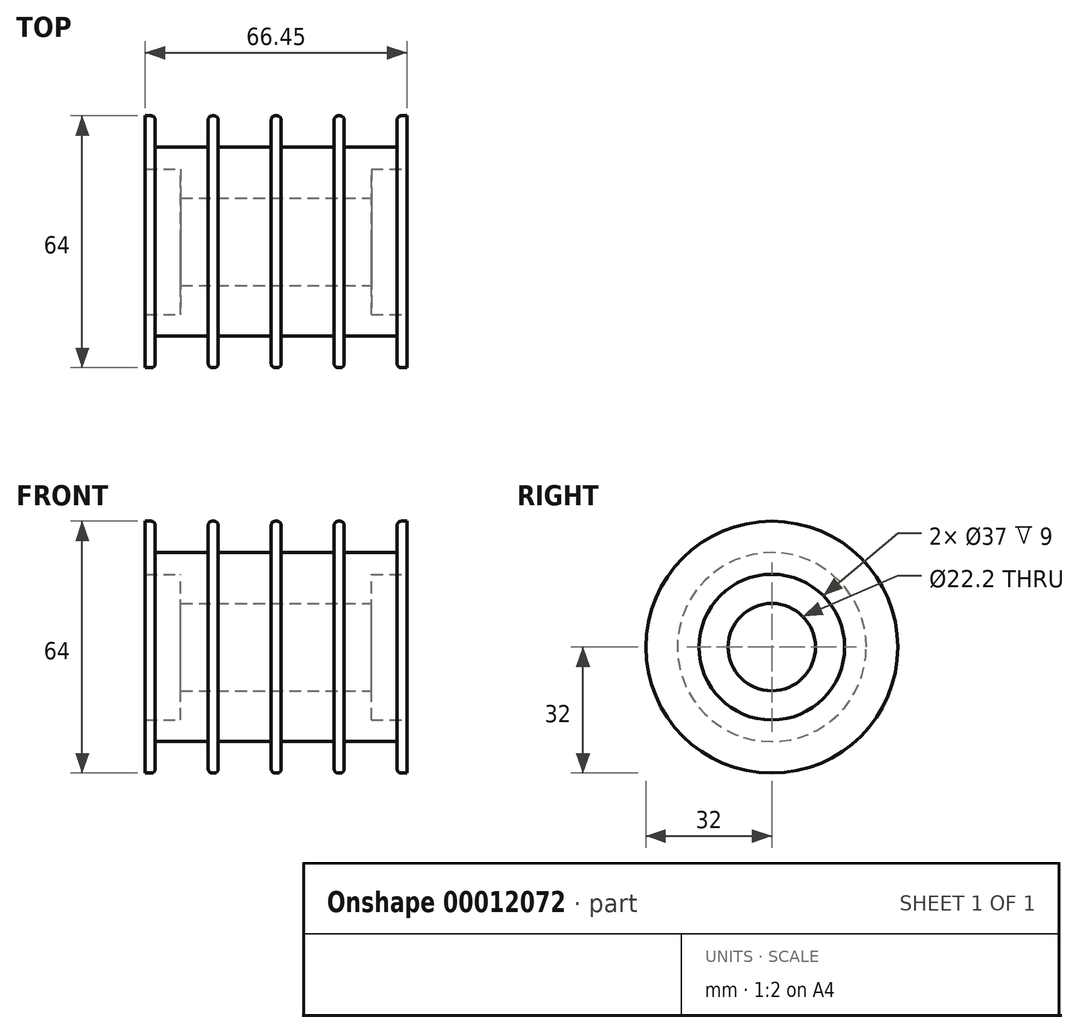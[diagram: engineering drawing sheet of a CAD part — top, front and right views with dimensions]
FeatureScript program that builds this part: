
annotation { "Feature Type Name" : "Feature", "Feature Type Description" : "" }
export const myFeature = defineFeature(function(context is Context, id is Id, definition is map)
    precondition{}
    {
        {
            var Q0;
            Q0=qCreatedBy(makeId("Front.planeOp"),FACE);
            var sketch = newSketch(context, id + "F0", { "sketchPlane" : qUnion([Q0])});
            skLineSegment(sketch, "E0.bottom", {"start": v(0, 0) * mm, "end": v(-66.45, 0) * mm, "construction": true});
            skLineSegment(sketch, "E0.left", {"start": v(0, 18.5) * mm, "end": v(0, 32) * mm});
            skLineSegment(sketch, "E1", {"start": v(-66.45, 32) * mm, "end": v(-66.45, 18.5) * mm});
            skLineSegment(sketch, "E2.0", {"start": v(-9, 11.1) * mm, "end": v(-57.45, 11.1) * mm});
            skLineSegment(sketch, "E3", {"start": v(0, 32) * mm, "end": v(-1.45, 32) * mm});
            skLineSegment(sketch, "E4", {"start": v(-2.45, 31) * mm, "end": v(-2.45, 24) * mm});
            skLineSegment(sketch, "E5", {"start": v(-2.45, 24) * mm, "end": v(-15.95, 24) * mm});
            skLineSegment(sketch, "E6", {"start": v(-15.95, 31) * mm, "end": v(-15.95, 24) * mm});
            skLineSegment(sketch, "E7", {"start": v(-18.45, 31) * mm, "end": v(-18.45, 24) * mm});
            skLineSegment(sketch, "E8", {"start": v(-31.95, 31) * mm, "end": v(-31.95, 24) * mm});
            skLineSegment(sketch, "E9", {"start": v(-34.45, 31) * mm, "end": v(-34.45, 24) * mm});
            skLineSegment(sketch, "E10", {"start": v(-47.95, 31) * mm, "end": v(-47.95, 24) * mm});
            skLineSegment(sketch, "E11", {"start": v(-50.45, 31) * mm, "end": v(-50.45, 24) * mm});
            skLineSegment(sketch, "E12", {"start": v(-63.95, 24) * mm, "end": v(-63.95, 31) * mm});
            skLineSegment(sketch, "E13.trimOffspring", {"start": v(-18.45, 24) * mm, "end": v(-31.95, 24) * mm});
            skLineSegment(sketch, "E14.trimOffspring", {"start": v(-16.95, 32) * mm, "end": v(-17.45, 32) * mm});
            skLineSegment(sketch, "E15.trimOffspring", {"start": v(-32.95, 32) * mm, "end": v(-33.45, 32) * mm});
            skLineSegment(sketch, "E16.trimOffspring", {"start": v(-34.45, 24) * mm, "end": v(-47.95, 24) * mm});
            skLineSegment(sketch, "E17.trimOffspring", {"start": v(-48.95, 32) * mm, "end": v(-49.45, 32) * mm});
            skLineSegment(sketch, "E18.trimOffspring", {"start": v(-50.45, 24) * mm, "end": v(-63.95, 24) * mm});
            skLineSegment(sketch, "E19.trimOffspring", {"start": v(-64.95, 32) * mm, "end": v(-66.45, 32) * mm});
            skLineSegment(sketch, "E20", {"start": v(-66.45, 18.5) * mm, "end": v(-57.45, 18.5) * mm});
            skLineSegment(sketch, "E21", {"start": v(-57.45, 18.5) * mm, "end": v(-57.45, 11.1) * mm});
            skLineSegment(sketch, "E22", {"start": v(0, 18.5) * mm, "end": v(-9, 18.5) * mm});
            skLineSegment(sketch, "E23", {"start": v(-9, 18.5) * mm, "end": v(-9, 11.1) * mm});
            skArc(sketch, "E24.filletArc", {"start": v(-63.95, 31) * mm, "mid": v(-64.24, 31.7) * mm, "end": v(-64.95, 32) * mm});
            skArc(sketch, "E25.filletArc", {"start": v(-49.45, 32) * mm, "mid": v(-50.15, 31.7) * mm, "end": v(-50.45, 31) * mm});
            skArc(sketch, "E26.filletArc", {"start": v(-47.95, 31) * mm, "mid": v(-48.24, 31.7) * mm, "end": v(-48.95, 32) * mm});
            skArc(sketch, "E27.filletArc", {"start": v(-33.45, 32) * mm, "mid": v(-34.15, 31.7) * mm, "end": v(-34.45, 31) * mm});
            skArc(sketch, "E28.filletArc", {"start": v(-31.95, 31) * mm, "mid": v(-32.24, 31.7) * mm, "end": v(-32.95, 32) * mm});
            skArc(sketch, "E29.filletArc", {"start": v(-17.45, 32) * mm, "mid": v(-18.15, 31.7) * mm, "end": v(-18.45, 31) * mm});
            skArc(sketch, "E30.filletArc", {"start": v(-15.95, 31) * mm, "mid": v(-16.24, 31.7) * mm, "end": v(-16.95, 32) * mm});
            skArc(sketch, "E31.filletArc", {"start": v(-1.45, 32) * mm, "mid": v(-2.15, 31.7) * mm, "end": v(-2.45, 31) * mm});
            skSolve(sketch);
        }
        {
            var Q0;
            Q0=qSketchRegion(id+"F0",true);
            var Q1;
            Q1=sQuery(id+"F0.wireOp",EDGE,"E0.bottom");
            revolve(context, id + "F1", {"entities" : qUnion([Q0]), "axis" : qUnion([Q1]), "revolveType" : RevolveType.FULL});
        }
    });
